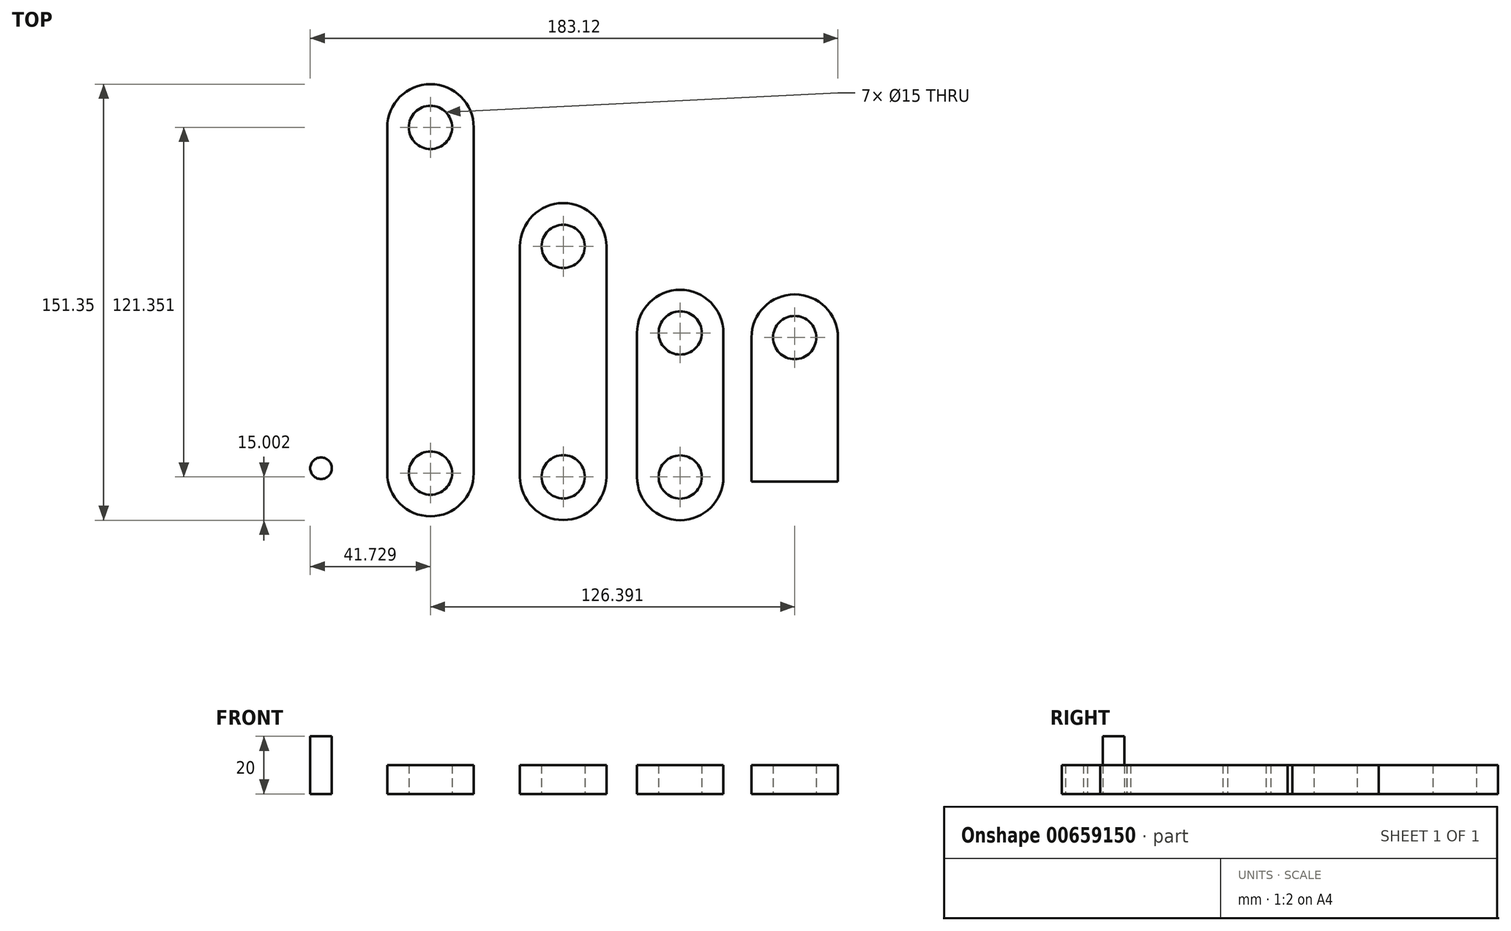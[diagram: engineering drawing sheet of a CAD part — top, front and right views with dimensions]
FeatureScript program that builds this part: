
annotation { "Feature Type Name" : "Feature", "Feature Type Description" : "" }
export const myFeature = defineFeature(function(context is Context, id is Id, definition is map)
    precondition{}
    {
        {
            assignVariable(context, id + "F0", {"name" : "thickness", "anyValue" : 10});
        }
        {
            var Q0;
            Q0=qCreatedBy(makeId("Top.planeOp"),FACE);
            var sketch = newSketch(context, id + "F1", { "sketchPlane" : qUnion([Q0])});
            skLineSegment(sketch, "E0.bottom", {"start": v(0, 0) * mm, "end": v(30, 0) * mm});
            skLineSegment(sketch, "E0.left", {"start": v(0, 0) * mm, "end": v(0, 50) * mm});
            skLineSegment(sketch, "E0.right", {"start": v(30, 0) * mm, "end": v(30, 50) * mm});
            skArc(sketch, "E1", {"start": v(30, 50) * mm, "mid": v(15, 65) * mm, "end": v(0, 50) * mm});
            skCircle(sketch, "E2", {"center": v(15, 50) * mm, "radius": 7.5 * mm});
            skSolve(sketch);
        }
        {
            var Q0;
            Q0=makeQuery(id+"F1.imprint","IMPRINT",FACE,{"disambiguationData":[TD([[makeQuery(id+"F1.imprint","IMPRINT",EDGE,{"derivedFrom":sQuery(id+"F1.wireOp",EDGE,"E0.bottom")}),1.0]])]});
            extrude(context, id + "F2", {"entities" : qUnion([Q0]), "depth" : (getVariable(context, 'thickness')) * mm, "offsetDistance" : 25 * mm});
        }
        {
            var Q0;
            Q0=qCreatedBy(makeId("Top.planeOp"),FACE);
            var sketch = newSketch(context, id + "F3", { "sketchPlane" : qUnion([Q0])});
            skLineSegment(sketch, "E3.left", {"start": v(-39.72, 1.6) * mm, "end": v(-39.72, 51.6) * mm});
            skLineSegment(sketch, "E3.right", {"start": v(-9.72, 1.6) * mm, "end": v(-9.72, 51.6) * mm});
            skArc(sketch, "E4", {"start": v(-9.72, 51.6) * mm, "mid": v(-24.72, 66.6) * mm, "end": v(-39.72, 51.6) * mm});
            skCircle(sketch, "E5", {"center": v(-24.72, 51.6) * mm, "radius": 7.5 * mm});
            skArc(sketch, "E6", {"start": v(-39.72, 1.6) * mm, "mid": v(-24.72, -13.4) * mm, "end": v(-9.72, 1.6) * mm});
            skCircle(sketch, "E7", {"center": v(-24.72, 1.6) * mm, "radius": 7.5 * mm});
            skSolve(sketch);
        }
        {
            var Q0;
            Q0=makeQuery(id+"F3.imprint","IMPRINT",FACE,{"disambiguationData":[TD([[makeQuery(id+"F3.imprint","IMPRINT",EDGE,{"derivedFrom":sQuery(id+"F3.wireOp",EDGE,"E3.left")}),-1.0]])]});
            extrude(context, id + "F4", {"entities" : qUnion([Q0]), "depth" : (getVariable(context, 'thickness')) * mm, "offsetDistance" : 25 * mm});
        }
        {
            var Q0;
            Q0=qCreatedBy(makeId("Top.planeOp"),FACE);
            var sketch = newSketch(context, id + "F5", { "sketchPlane" : qUnion([Q0])});
            skLineSegment(sketch, "E8.left", {"start": v(-80.33, 1.67) * mm, "end": v(-80.33, 81.67) * mm});
            skLineSegment(sketch, "E8.right", {"start": v(-50.33, 1.67) * mm, "end": v(-50.33, 81.67) * mm});
            skArc(sketch, "E9", {"start": v(-50.33, 81.67) * mm, "mid": v(-65.33, 96.67) * mm, "end": v(-80.33, 81.67) * mm});
            skCircle(sketch, "E10", {"center": v(-65.33, 81.67) * mm, "radius": 7.5 * mm});
            skArc(sketch, "E11", {"start": v(-80.33, 1.67) * mm, "mid": v(-65.33, -13.33) * mm, "end": v(-50.33, 1.67) * mm});
            skCircle(sketch, "E12", {"center": v(-65.33, 1.67) * mm, "radius": 7.5 * mm});
            skSolve(sketch);
        }
        {
            var Q0;
            Q0=makeQuery(id+"F5.imprint","IMPRINT",FACE,{"disambiguationData":[TD([[makeQuery(id+"F5.imprint","IMPRINT",EDGE,{"derivedFrom":sQuery(id+"F5.wireOp",EDGE,"E8.left")}),-1.0]])]});
            extrude(context, id + "F6", {"entities" : qUnion([Q0]), "depth" : (getVariable(context, 'thickness')) * mm, "offsetDistance" : 25 * mm});
        }
        {
            var Q0;
            Q0=qCreatedBy(makeId("Top.planeOp"),FACE);
            var sketch = newSketch(context, id + "F7", { "sketchPlane" : qUnion([Q0])});
            skLineSegment(sketch, "E13.left", {"start": v(-126.4, 2.95) * mm, "end": v(-126.4, 122.95) * mm});
            skLineSegment(sketch, "E13.right", {"start": v(-96.4, 2.95) * mm, "end": v(-96.4, 122.95) * mm});
            skArc(sketch, "E14", {"start": v(-96.4, 122.95) * mm, "mid": v(-111.4, 137.95) * mm, "end": v(-126.4, 122.95) * mm});
            skCircle(sketch, "E15", {"center": v(-111.4, 122.95) * mm, "radius": 7.5 * mm});
            skArc(sketch, "E16", {"start": v(-126.4, 2.95) * mm, "mid": v(-111.4, -12.05) * mm, "end": v(-96.4, 2.95) * mm});
            skCircle(sketch, "E17", {"center": v(-111.4, 2.95) * mm, "radius": 7.5 * mm});
            skSolve(sketch);
        }
        {
            var Q0;
            Q0=makeQuery(id+"F7.imprint","IMPRINT",FACE,{"disambiguationData":[TD([[makeQuery(id+"F7.imprint","IMPRINT",EDGE,{"derivedFrom":sQuery(id+"F7.wireOp",EDGE,"E13.left")}),-1.0]])]});
            extrude(context, id + "F8", {"entities" : qUnion([Q0]), "depth" : (getVariable(context, 'thickness')) * mm, "offsetDistance" : 25 * mm});
        }
        {
            var Q0;
            Q0=qCreatedBy(makeId("Top.planeOp"),FACE);
            var sketch = newSketch(context, id + "F9", { "sketchPlane" : qUnion([Q0])});
            skCircle(sketch, "E18", {"center": v(-149.37, 4.64) * mm, "radius": 3.75 * mm});
            skSolve(sketch);
        }
        {
            var Q0;
            Q0=makeQuery(id+"F9.imprint","IMPRINT",FACE,{"disambiguationData":[TD([[makeQuery(id+"F9.imprint","IMPRINT",EDGE,{"derivedFrom":sQuery(id+"F9.wireOp",EDGE,"E18")}),1.0]])]});
            extrude(context, id + "F10", {"entities" : qUnion([Q0]), "depth" : (getVariable(context, 'thickness') * 2) * mm, "offsetDistance" : 25 * mm});
        }
    });
